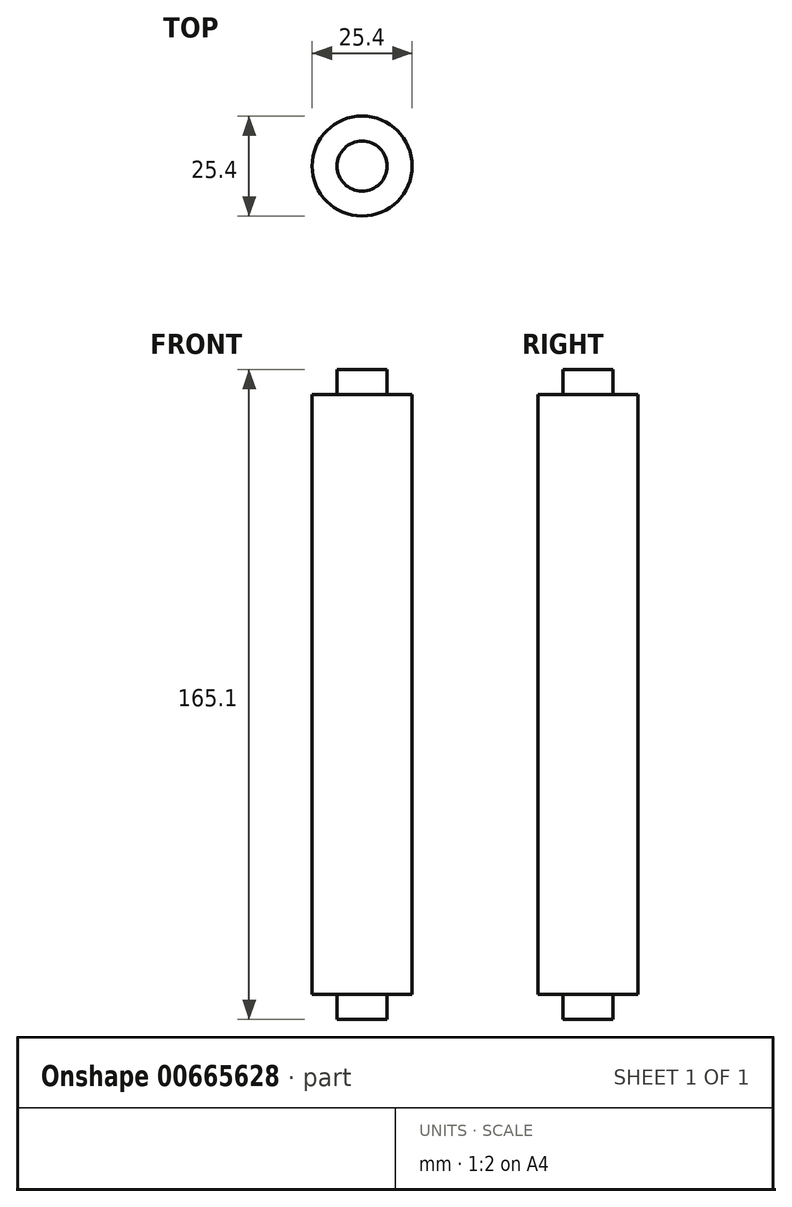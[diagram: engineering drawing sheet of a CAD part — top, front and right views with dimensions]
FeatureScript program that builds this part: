
annotation { "Feature Type Name" : "Feature", "Feature Type Description" : "" }
export const myFeature = defineFeature(function(context is Context, id is Id, definition is map)
    precondition{}
    {
        {
            var Q0;
            Q0=qCreatedBy(makeId("Top.planeOp"),FACE);
            var sketch = newSketch(context, id + "F0", { "sketchPlane" : qUnion([Q0])});
            skCircle(sketch, "E0", {"center": v(0, 0) * mm, "radius": 12.7 * mm});
            skSolve(sketch);
        }
        {
            var Q0;
            Q0 = qSketchRegion(id + "F0", true);
            extrude(context, id + "F1", {"entities" : qUnion([Q0]), "endBound" : BoundingType.SYMMETRIC, "depth" : 152.4 * mm, "offsetDistance" : 25.4 * mm});
        }
        {
            var Q0;
            Q0=qCreatedBy(makeId("Top.planeOp"),FACE);
            var sketch = newSketch(context, id + "F2", { "sketchPlane" : qUnion([Q0])});
            skCircle(sketch, "E1", {"center": v(0, 0) * mm, "radius": 6.35 * mm});
            skSolve(sketch);
        }
        {
            var Q0;
            Q0 = qSketchRegion(id + "F2", true);
            extrude(context, id + "F3", {"entities" : qUnion([Q0]), "operationType" : NewBodyOperationType.ADD, "endBound" : BoundingType.SYMMETRIC, "depth" : 165.1 * mm, "offsetDistance" : 25.4 * mm});
        }
    });
